# Revit family: MINI UNDERWATER 3W SIMETRICA_LKS01WW.30_CW.30
name_source: partatom
category: Luminarias
units: mm (PartAtom-declared; Revit-internal decimal feet)

## family parameters
Compartido = No
Corte con vacíos al cargar = No
Cota de conector redondo = Diámetro de uso
Origen de luz = Sí
Punto de cálculo de habitación = No
Se basa en plano de trabajo = Sí
Siempre vertical = No
Tipo de pieza = Normal

## types (2) — shared parameters
Cambio de temperatura de color de luz atenuada = <Ninguno>
Comentarios de vataje = 24V
Fabricante = BRILLANT
Filtro de color = 16777215
Longitud de símbolo de origen de luz = 500 mm  [stored 1.64042 ft]
Lámpara = OSRAM
Watt per fixture = 3
Ángulo de campo de foco = 30.00°
Ángulo de enfoque = 30.00°
Ángulo de inclinación = 30.00°
zero-valued in all types: Elevación por defecto

## per-type parameters (varying)
| type | Descripción | Modelo |
| SUB_LKSC01WW.30 | LUMINARIA SUB ACUATICA TIPO PUNTUAL PARA EMPOTRAR EN PISO 68.5MM DE DIAMETRO POR 135MM DE ALTO CONSIDERANDO EL HOUSING, ACABADO EN ACERO INOXIDABLE, CUERPO MOLDEADO EN CROMO, SELLO DE SILICON, VIDRIO TEMPLADO DE 7MM, 1 LED TIPO OSRAM CON UN CONSUMO TOTAL DE 3 W, 139 LUMENES, CON UNA TEMPERATURA EN BLANCO CALIDO 3000K , IP 68, IK 08, SUMERGIBLE MAXIMO 2M, CABLE H07RN DE 3M, APERTURA EN STOCK A 30 GRADOS, ALIMENTADA A 24V. REQUIERE ACCESORIOS. | LKSC01WW.30 |
| SUB_LKSC01CW.30 | LUMINARIA SUB ACUATICA TIPO PUNTUAL PARA EMPOTRAR EN PISO 68.5MM DE DIAMETRO POR 135MM DE ALTO CONSIDERANDO EL HOUSING, ACABADO EN ACERO INOXIDABLE, CUERPO MOLDEADO EN CROMO, SELLO DE SILICON, VIDRIO TEMPLADO DE 7MM, 1 LED TIPO OSRAM CON UN CONSUMO TOTAL DE 3 W, 174 LUMENES, CON UNA TEMPERATURA EN BLANCO FRIO 6000K , IP 68, IK 08, SUMERGIBLE MAXIMO 2M, CABLE H07RN DE 3M, APERTURA EN STOCK A 30 GRADOS, ALIMENTADA A 24V. REQUIERE ACCESORIOS. | LKSC01CW.30 |

note: [stored X ft] marks values corroborated as IEEE doubles in the binary element streams (Revit-internal decimal feet)

## geometry (parser evidence)
native form markers: Blend x2
no freeform markers — native parametric forms only
